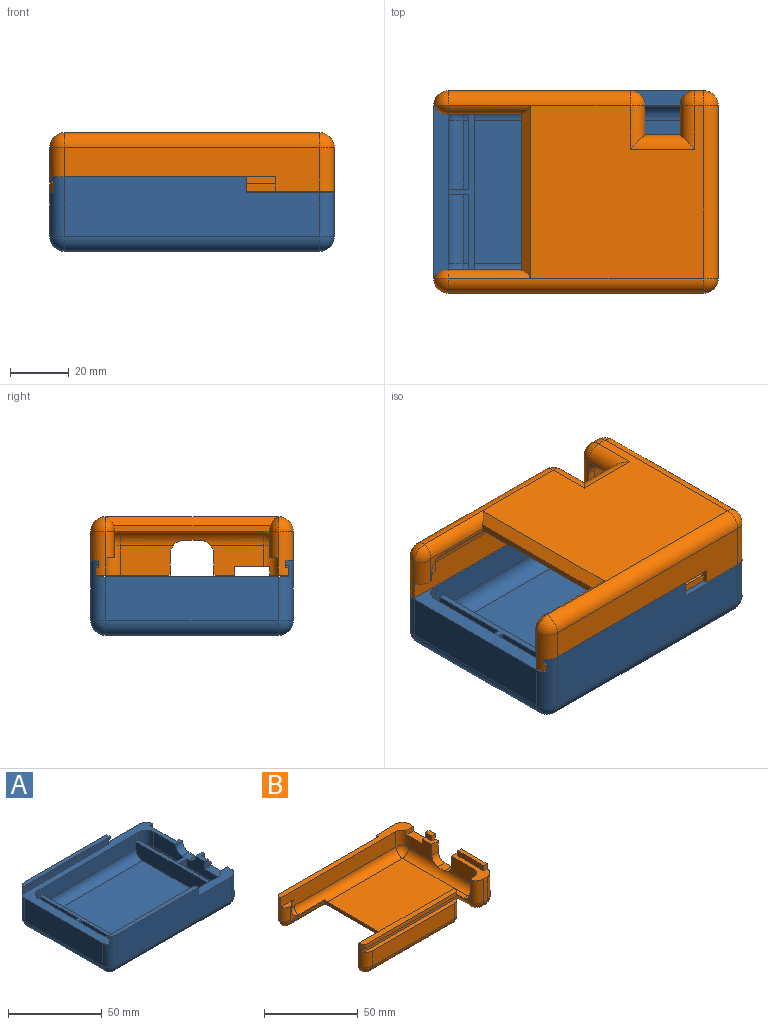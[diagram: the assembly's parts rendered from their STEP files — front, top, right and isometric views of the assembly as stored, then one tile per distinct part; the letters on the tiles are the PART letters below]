
ASSEMBLY  parts=2 mates=1
PART A: 90 faces, bbox 97x69x25.5 mm
  f0: plane 43x43mm, normal (0,0,-1), area 1018.6mm2, adj f83,f84,f86,f87,f89
  f1: cylinder r=5mm len=20.5mm, axis (0,0,-1), area 141.6mm2, adj f5,f24,f25,f35,f74,f79,f80,f81
  f2: cylinder r=5mm len=20.5mm, axis (0,0,1), area 141.6mm2, adj f4,f5,f23,f25,f38,f76,f77,f78
  f3: plane 5.5x2.5mm, normal (1,0,0), area 9.8mm2, adj f5,f24,f74,f79,f80,f81
  f4: plane 66.33x2.5mm, normal (0,0,1), area 162.7mm2, adj f2,f23,f75,f76
  f5: plane 97.01x69.01mm, normal (0,0,1), area 1146mm2, adj f1,f2,f3,f7,f8,f11,f17,f23
  f6: plane 5x5mm, normal (0,-1,0), area 17.1mm2, adj f7,f9,f10,f64,f72,f73
  f7: plane 59x15mm, normal (1,0,0), area 682mm2, adj f5,f6,f8,f10,f31,f32,f62,f63
  f8: cylinder r=5mm len=15mm, axis (0,0,1), area 117.3mm2, adj f5,f7,f24,f30,f67,f70
  f9: plane 23.53x10mm, normal (-1,0,0), area 158mm2, adj f6,f10,f14,f39,f58,f62,f64,f65
  f10: plane 7x5mm, normal (0,0,1), area 22.5mm2, adj f6,f7,f9,f65,f71,f72
  f11: plane 77x10mm, normal (0,1,0), area 750mm2, adj f5,f15,f20,f39,f43,f44,f51,f52
  f12: plane 23.53x1mm, normal (0,0,1), area 23.5mm2, adj f14,f43,f58,f59
  f13: plane 70x49mm, normal (0,0,1), area 3430mm2, adj f15,f16,f51,f57
  f14: cylinder r=5mm len=23.53mm, axis (0,1,0), area 184.8mm2, adj f9,f12,f40,f58
  f15: cylinder r=5mm len=70mm, axis (1,0,0), area 549.8mm2, adj f11,f13,f51,f57
  f16: cylinder r=5mm len=70mm, axis (-1,0,0), area 549.8mm2, adj f13,f27,f51,f57
  f17: plane 49x10mm, normal (1,0,0), area 480mm2, adj f5,f22,f44,f48,f50,f53,f54,f56
  f18: plane 23.53x2mm, normal (0,0,1), area 47.1mm2, adj f20,f22,f52,f53
  f19: plane 23.47x2mm, normal (0,0,1), area 46.9mm2, adj f21,f48,f54,f55
  f20: cylinder r=5mm len=5mm, axis (1,0,0), area 15.7mm2, adj f11,f18,f46,f52
  f21: cylinder r=5mm len=5mm, axis (-1,0,0), area 15.7mm2, adj f19,f27,f49,f55
  f22: cylinder r=5mm len=23.53mm, axis (0,-1,0), area 184.8mm2, adj f17,f18,f46,f53
  f23: plane 87x20.5mm, normal (0,-1,0), area 1646mm2, adj f2,f4,f5,f31,f36,f75
  f24: plane 87x20.5mm, normal (0,1,0), area 1646mm2, adj f1,f3,f5,f8,f33,f74
  f25: plane 59x15mm, normal (-1,0,0), area 885mm2, adj f1,f2,f5,f37
  f26: plane 87x59mm, normal (0,0,-1), area 3542.6mm2, adj f32,f33,f36,f37,f82
  f27: plane 77x10mm, normal (0,-1,0), area 750mm2, adj f5,f16,f21,f41,f47,f50,f51,f55
  f28: plane 23.47x10mm, normal (-1,0,0), area 207.7mm2, adj f5,f41,f42,f61,f62,f66
  f29: plane 23.47x1mm, normal (0,0,1), area 23.5mm2, adj f42,f47,f60,f61
  f30: sphere r=5mm, area 39.3mm2, adj f8,f32,f33
  f31: cylinder r=5mm len=15mm, axis (0,0,-1), area 117.8mm2, adj f5,f7,f23,f34
  f32: cylinder r=5mm len=59mm, axis (0,-1,0), area 463.4mm2, adj f7,f26,f30,f34
  f33: cylinder r=5mm len=87mm, axis (1,0,0), area 683.3mm2, adj f24,f26,f30,f35
  f34: sphere r=5mm, area 39.3mm2, adj f31,f32,f36
  f35: sphere r=5mm, area 39.3mm2, adj f1,f33,f37
  f36: cylinder r=5mm len=87mm, axis (-1,0,0), area 683.3mm2, adj f23,f26,f34,f38
  f37: cylinder r=5mm len=59mm, axis (0,1,0), area 463.4mm2, adj f25,f26,f35,f38
  f38: sphere r=5mm, area 39.3mm2, adj f2,f36,f37
  f39: cylinder r=5mm len=10mm, axis (0,0,1), area 68.3mm2, adj f5,f9,f11,f40,f63,f64
  f40: sphere r=5mm, area 39.3mm2, adj f14,f39,f43
  f41: cylinder r=5mm len=10mm, axis (0,0,-1), area 78.5mm2, adj f5,f27,f28,f45
  f42: cylinder r=5mm len=23.47mm, axis (0,1,0), area 184.4mm2, adj f28,f29,f45,f61
  f43: cylinder r=5mm len=5mm, axis (1,0,0), area 7.9mm2, adj f11,f12,f40,f59
  f44: cylinder r=5mm len=10mm, axis (0,0,-1), area 78.5mm2, adj f5,f11,f17,f46
  f45: sphere r=5mm, area 39.3mm2, adj f41,f42,f47
  f46: sphere r=5mm, area 39.3mm2, adj f20,f22,f44
  f47: cylinder r=5mm len=5mm, axis (-1,0,0), area 7.9mm2, adj f27,f29,f45,f60
  f48: cylinder r=5mm len=23.47mm, axis (0,-1,0), area 184.4mm2, adj f17,f19,f49,f54
  f49: sphere r=5mm, area 39.3mm2, adj f21,f48,f50
  f50: cylinder r=5mm len=10mm, axis (0,0,1), area 78.5mm2, adj f5,f17,f27,f49
  f51: plane 59x10mm, normal (1,0,0), area 579.3mm2, adj f11,f13,f15,f16,f27,f56
  f52: plane 28.53x10mm, normal (-1,0,0), area 279.9mm2, adj f11,f18,f20,f53,f56
  f53: plane 10x7mm, normal (0,-1,0), area 64.6mm2, adj f17,f18,f22,f52,f56
  f54: plane 10x7mm, normal (0,1,0), area 64.6mm2, adj f17,f19,f48,f55,f56
  f55: plane 28.47x10mm, normal (-1,0,0), area 279.4mm2, adj f19,f21,f27,f54,f56
  f56: plane 59x9mm, normal (0,0,1), area 132mm2, adj f11,f17,f27,f51,f52,f53,f54,f55
  f57: plane 59x10mm, normal (-1,0,0), area 579.3mm2, adj f11,f13,f15,f16,f27,f62
  f58: plane 10x6mm, normal (0,-1,0), area 54.6mm2, adj f9,f12,f14,f59,f62
  f59: plane 28.53x10mm, normal (1,0,0), area 279.9mm2, adj f11,f12,f43,f58,f62
  f60: plane 28.47x10mm, normal (1,0,0), area 279.4mm2, adj f27,f29,f47,f61,f62
  f61: plane 10x6mm, normal (0,1,0), area 54.6mm2, adj f28,f29,f42,f60,f62
  f62: plane 59x13mm, normal (0,0,1), area 155mm2, adj f7,f9,f11,f27,f28,f57,f58,f59
  f63: plane 5.42x5mm, normal (0,1,0), area 27.1mm2, adj f5,f7,f39,f64
  f64: plane 12x5.42mm, normal (0,0,1), area 60.3mm2, adj f6,f7,f9,f39,f63
  f65: cylinder r=5mm len=5mm, axis (-1,0,0), area 39.3mm2, adj f7,f9,f10,f62
  f66: cylinder r=5mm len=5mm, axis (1,0,0), area 39.3mm2, adj f5,f7,f28,f62
  f67: plane 3.15x2.5mm, normal (0,-1,0), area 7.9mm2, adj f5,f8,f68,f70
  f68: plane 20.15x3.15mm, normal (1,0,0), area 63.5mm2, adj f5,f67,f69,f70
  f69: plane 3.15x2.5mm, normal (0,1,0), area 7.9mm2, adj f5,f7,f68,f70
  f70: plane 20.15x2.5mm, normal (0,0,1), area 50.4mm2, adj f7,f8,f67,f68,f69
  f71: plane 3.15x2.5mm, normal (0,-1,0), area 7.9mm2, adj f7,f10,f72,f73
  f72: plane 5x3.15mm, normal (1,0,0), area 15.8mm2, adj f6,f10,f71,f73
  f73: plane 5x2.5mm, normal (0,0,1), area 12.5mm2, adj f6,f7,f71,f72
  f74: plane 66.33x2.5mm, normal (0,0,1), area 162.7mm2, adj f1,f3,f24,f81
  f75: plane 5.5x2.5mm, normal (1,0,0), area 9.8mm2, adj f4,f5,f23,f76,f77,f78
  f76: plane 66.33x1.5mm, normal (0,1,0), area 99.5mm2, adj f2,f4,f75,f77
  f77: plane 66.33x1mm, normal (0,0,-1), area 66mm2, adj f2,f75,f76,f78
  f78: plane 65.57x4mm, normal (0,1,0), area 262.3mm2, adj f2,f5,f75,f77
  f79: plane 65.57x4mm, normal (0,-1,0), area 262.3mm2, adj f1,f3,f5,f80
  f80: plane 66.33x1mm, normal (0,0,-1), area 66mm2, adj f1,f3,f79,f81
  f81: plane 66.33x1.5mm, normal (0,-1,0), area 99.5mm2, adj f1,f3,f74,f80
  f82: cylinder r=22.5mm len=45mm, axis (0,0,-1), area 141.4mm2, adj f26,f89
  f83: extruded ~11.24x9.76mm, area 72.2mm2, adj f0,f84,f85
  f84: extruded ~24.86x10.79mm, area 117.6mm2, adj f0,f83,f85
  f85: plane 34.29x13.91mm, normal (0,0,-1), area 215.6mm2, adj f83,f84
  f86: extruded ~11.21x9.74mm, area 74.5mm2, adj f0,f87,f88
  f87: extruded ~24.75x10.84mm, area 115.7mm2, adj f0,f86,f88
  f88: plane 34.32x13.85mm, normal (0,0,-1), area 217.7mm2, adj f86,f87
  f89: torus R=21.5mm, axis (0,0,-1), area 218.5mm2, adj f0,f82
PART B: 84 faces, bbox 97x69x23.4 mm
  f0: plane 62x10mm, normal (0,-1,0), area 620mm2, adj f33,f35,f51,f74
  f1: plane 87x15mm, normal (0,1,0), area 945mm2, adj f2,f5,f26,f30,f75,f79
  f2: plane 97x8mm, normal (0,0,1), area 382.7mm2, adj f1,f5,f22,f23,f26,f41,f78,f79
  f3: cylinder r=5mm len=4.58mm, axis (0,0,-1), area 23.2mm2, adj f7,f20,f24,f69
  f4: plane 72x3.5mm, normal (0,0,1), area 248.9mm2, adj f24,f35,f51,f71
  f5: cylinder r=5mm len=15mm, axis (0,0,-1), area 94.8mm2, adj f1,f2,f9,f23,f32,f75,f76,f77
  f6: cylinder r=5mm len=4.58mm, axis (0,0,1), area 23.2mm2, adj f8,f23,f38,f70
  f7: plane 25.42x9.42mm, normal (0,1,0), area 32.9mm2, adj f3,f10,f19,f20,f47,f60,f61,f69
  f8: plane 25.42x9.42mm, normal (0,-1,0), area 32.9mm2, adj f6,f9,f37,f38,f47,f58,f59,f70
  f9: cylinder r=5mm len=9mm, axis (0,0,1), area 52.2mm2, adj f5,f8,f59,f70
  f10: cylinder r=5mm len=9mm, axis (0,0,1), area 52.2mm2, adj f7,f35,f61,f69
  f11: plane 27x13mm, normal (0,0,1), area 120.8mm2, adj f14,f16,f22,f25,f28,f43,f57,f65
  f12: plane 7x5mm, normal (0,0,1), area 23.2mm2, adj f21,f22,f39,f44,f62,f63
  f13: cylinder r=5mm len=5mm, axis (1,0,0), area 23.6mm2, adj f16,f18,f50,f81
  f14: plane 15x3mm, normal (0,-1,0), area 45mm2, adj f11,f17,f28,f57
  f15: plane 59x59mm, normal (0,0,-1), area 3151mm2, adj f17,f29,f30,f33,f48,f53,f54,f55
  f16: plane 10x3mm, normal (0,1,0), area 30mm2, adj f11,f13,f57,f80
  f17: cylinder r=5mm len=5mm, axis (-1,0,0), area 23.6mm2, adj f14,f15,f31,f56
  f18: plane 57x49mm, normal (0,0,1), area 2733mm2, adj f13,f19,f36,f37,f47,f53,f54,f55
  f19: cylinder r=5mm len=62mm, axis (1,0,0), area 445.8mm2, adj f7,f18,f20,f24,f47,f49
  f20: sphere r=5mm, area 23.6mm2, adj f3,f7,f19
  f21: plane 18x10mm, normal (-1,0,0), area 141mm2, adj f12,f36,f39,f40,f44,f46,f82
  f22: plane 59x18.35mm, normal (1,0,0), area 761mm2, adj f2,f11,f12,f26,f28,f29,f39,f40
  f23: plane 87x10mm, normal (0,-1,0), area 830mm2, adj f2,f5,f6,f37,f70,f82
  f24: plane 72x10mm, normal (0,1,0), area 680mm2, adj f3,f4,f19,f35,f51,f69
  f25: plane 18x10mm, normal (-1,0,0), area 171mm2, adj f11,f36,f43,f45,f80
  f26: cylinder r=5mm len=15mm, axis (0,0,1), area 117.8mm2, adj f1,f2,f22,f27
  f27: sphere r=5mm, area 39.3mm2, adj f26,f29,f30
  f28: cylinder r=5mm len=15mm, axis (0,0,-1), area 117.8mm2, adj f11,f14,f22,f31
  f29: cylinder r=5mm len=59mm, axis (0,-1,0), area 463.4mm2, adj f15,f22,f27,f31
  f30: cylinder r=5mm len=87mm, axis (1,0,0), area 683.3mm2, adj f1,f15,f27,f32,f58
  f31: sphere r=5mm, area 39.3mm2, adj f17,f28,f29
  f32: sphere r=5mm, area 39.3mm2, adj f5,f30,f59
  f33: cylinder r=5mm len=62mm, axis (-1,0,0), area 486.9mm2, adj f0,f15,f34,f52,f60
  f34: sphere r=5mm, area 39.3mm2, adj f33,f35,f61
  f35: cylinder r=5mm len=15mm, axis (0,0,1), area 94.8mm2, adj f0,f4,f10,f24,f34,f71,f72,f73
  f36: cylinder r=5mm len=49mm, axis (0,1,0), area 363.2mm2, adj f18,f21,f25,f42,f45,f46,f81,f83
  f37: cylinder r=5mm len=77mm, axis (-1,0,0), area 563.6mm2, adj f8,f18,f23,f38,f47,f83
  f38: sphere r=5mm, area 23.6mm2, adj f6,f8,f37
  f39: plane 6.35x5mm, normal (0,1,0), area 23.4mm2, adj f12,f21,f22,f40,f63,f64
  f40: plane 12x5.42mm, normal (0,0,1), area 60.3mm2, adj f21,f22,f39,f41,f82
  f41: plane 5.42x3mm, normal (0,-1,0), area 16.3mm2, adj f2,f22,f40,f82
  f42: plane 5.42x5mm, normal (0,0,1), area 27.1mm2, adj f22,f36,f45,f46
  f43: plane 7x5mm, normal (0,1,0), area 35mm2, adj f11,f22,f25,f45
  f44: plane 7x5mm, normal (0,-1,0), area 35mm2, adj f12,f21,f22,f46
  f45: cylinder r=5mm len=5.42mm, axis (-1,0,0), area 40.3mm2, adj f22,f25,f36,f42,f43
  f46: cylinder r=5mm len=5.42mm, axis (1,0,0), area 40.3mm2, adj f21,f22,f36,f42,f44
  f47: plane 53.51x2.42mm, normal (-1,0,0), area 106.8mm2, adj f7,f8,f18,f19,f37,f48,f58,f60
  f48: plane 59x3mm, normal (-0.71,0,-0.71), area 235.3mm2, adj f15,f47,f58,f60
  f49: plane 5x5mm, normal (1,0,0), area 5.4mm2, adj f19,f51,f53
  f50: plane 5x5mm, normal (-1,0,0), area 5.4mm2, adj f13,f55,f57
  f51: cylinder r=5mm len=15mm, axis (0,0,1), area 94.8mm2, adj f0,f4,f24,f49,f52,f71,f72,f73
  f52: sphere r=5mm, area 39.3mm2, adj f33,f51,f53
  f53: cylinder r=5mm len=15mm, axis (0,1,0), area 92.8mm2, adj f15,f18,f49,f52,f54
  f54: cylinder r=5mm len=22mm, axis (1,0,0), area 122.8mm2, adj f15,f18,f53,f55
  f55: cylinder r=5mm len=15mm, axis (0,-1,0), area 92.8mm2, adj f15,f18,f50,f54,f56
  f56: sphere r=5mm, area 39.3mm2, adj f17,f55,f57
  f57: cylinder r=5mm len=15mm, axis (0,0,-1), area 117.8mm2, adj f11,f14,f16,f50,f56
  f58: cylinder r=5mm len=28mm, axis (-1,0,0), area 152mm2, adj f8,f30,f47,f48,f59
  f59: torus R=0.42mm, axis (0,-1,0), area 27.4mm2, adj f8,f9,f32,f58
  f60: cylinder r=5mm len=28mm, axis (-1,0,0), area 152mm2, adj f7,f33,f47,f48,f61
  f61: torus R=0.42mm, axis (0,-1,0), area 27.4mm2, adj f7,f10,f34,f60
  f62: plane 3.35x2.5mm, normal (0,-1,0), area 8.4mm2, adj f12,f22,f63,f64
  f63: plane 4.7x3.35mm, normal (-1,0,0), area 15.7mm2, adj f12,f39,f62,f64
  f64: plane 4.7x2.5mm, normal (0,0,1), area 11.8mm2, adj f22,f39,f62,f63
  f65: plane 3.35x2.5mm, normal (0,1,0), area 8.4mm2, adj f11,f22,f66,f68
  f66: plane 19.55x3.35mm, normal (-1,0,0), area 65.5mm2, adj f11,f65,f67,f68
  f67: plane 3.35x2.5mm, normal (0,-1,0), area 8.4mm2, adj f11,f22,f66,f68
  f68: plane 19.55x2.5mm, normal (0,0,1), area 48.9mm2, adj f22,f65,f66,f67
  f69: plane 10x3mm, normal (0,0,1), area 16.3mm2, adj f3,f7,f10,f24
  f70: plane 10x3mm, normal (0,0,1), area 16.3mm2, adj f6,f8,f9,f23
  f71: plane 69.14x2.5mm, normal (0,-1,0), area 172.9mm2, adj f4,f35,f51,f72
  f72: plane 70.66x1mm, normal (0,0,-1), area 70mm2, adj f35,f51,f71,f73
  f73: plane 70.66x2.5mm, normal (0,-1,0), area 176.7mm2, adj f35,f51,f72,f74
  f74: plane 70.66x2.5mm, normal (0,0,1), area 170.4mm2, adj f0,f35,f51,f73
  f75: plane 76.33x2.5mm, normal (0,0,1), area 187.7mm2, adj f1,f5,f76,f79
  f76: plane 76.33x2.5mm, normal (0,1,0), area 190.8mm2, adj f5,f75,f77,f79
  f77: plane 76.33x1mm, normal (0,0,-1), area 76mm2, adj f5,f76,f78,f79
  f78: plane 75.57x2.5mm, normal (0,1,0), area 188.9mm2, adj f2,f5,f77,f79
  f79: plane 5x2.5mm, normal (-1,0,0), area 10mm2, adj f1,f2,f75,f76,f77,f78
  f80: cylinder r=5mm len=10mm, axis (0,0,1), area 78.5mm2, adj f11,f16,f25,f81
  f81: sphere r=5mm, area 39.3mm2, adj f13,f36,f80
  f82: cylinder r=5mm len=10mm, axis (0,0,-1), area 72.4mm2, adj f2,f21,f23,f40,f41,f83
  f83: sphere r=5mm, area 39.3mm2, adj f36,f37,f82
PLACE A t=(12.61,-28.55,35.38)mm
PLACE B rot(axis=(-1,0,0),180deg) t=(12.61,-28.55,35.88)mm
MATE fastened B.f75 <-> A.f4  axis (0,0,-1) through (-83.72,-60.55,40.88)mm
